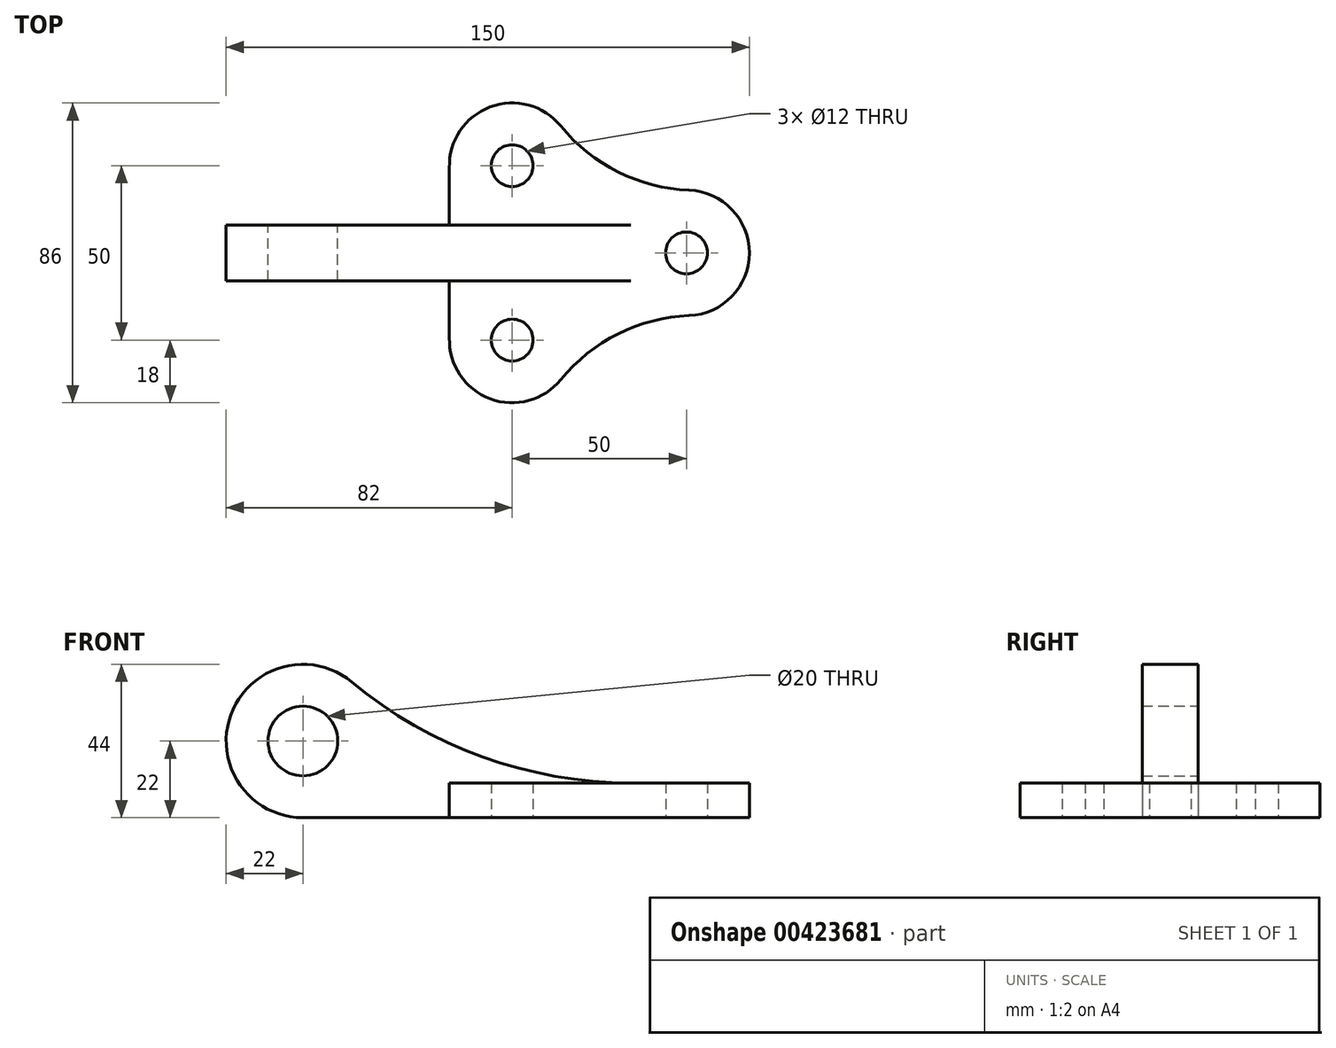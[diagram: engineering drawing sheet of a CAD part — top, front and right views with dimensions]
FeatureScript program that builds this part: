
annotation { "Feature Type Name" : "Feature", "Feature Type Description" : "" }
export const myFeature = defineFeature(function(context is Context, id is Id, definition is map)
    precondition{}
    {
        {
            var Q0;
            Q0=qCreatedBy(makeId("Top.planeOp"),FACE);
            var sketch = newSketch(context, id + "F0", { "sketchPlane" : qUnion([Q0])});
            skCircle(sketch, "E0", {"center": v(0, 0) * mm, "radius": 18 * mm});
            skCircle(sketch, "E1", {"center": v(-50, 25) * mm, "radius": 18 * mm});
            skCircle(sketch, "E2", {"center": v(-50, -25) * mm, "radius": 18 * mm});
            skLineSegment(sketch, "E3", {"start": v(-50, 25) * mm, "end": v(-50, -25) * mm});
            skLineSegment(sketch, "E4", {"start": v(0, 0) * mm, "end": v(-50, 0) * mm});
            skLineSegment(sketch, "E5", {"start": v(-68, 24.41) * mm, "end": v(-68, -25.59) * mm});
            skArc(sketch, "E6.MirrorCS", {"start": v(0.72, 17.99) * mm, "mid": v(-19.64, 23.22) * mm, "end": v(-36.04, 36.37) * mm});
            skCircle(sketch, "E7", {"center": v(-50, 25) * mm, "radius": 6 * mm});
            skCircle(sketch, "E8", {"center": v(-50, -25) * mm, "radius": 6 * mm});
            skCircle(sketch, "E9", {"center": v(0, 0) * mm, "radius": 6 * mm});
            skArc(sketch, "E10", {"start": v(0.72, -17.99) * mm, "mid": v(-19.64, -23.22) * mm, "end": v(-36.04, -36.37) * mm});
            skSolve(sketch);
        }
        {
            var Q0;
            Q0 = qSketchRegion(id + "F0", true);
            extrude(context, id + "F1", {"entities" : qUnion([Q0]), "depth" : 10 * mm});
        }
        {
            var Q0;
            Q0=qCreatedBy(makeId("Front.planeOp"),FACE);
            var sketch = newSketch(context, id + "F2", { "sketchPlane" : qUnion([Q0])});
            skCircle(sketch, "E11", {"center": v(-110, 22) * mm, "radius": 22 * mm});
            skLineSegment(sketch, "E12", {"start": v(0, 0) * mm, "end": v(-110.13, 0) * mm});
            skArc(sketch, "E13", {"start": v(-95.93, 38.91) * mm, "mid": v(-58.49, 17.45) * mm, "end": v(-15.98, 10) * mm});
            skPoint(sketch, "E14.orphan", {"position": v(0.72, 10) * mm});
            skLineSegment(sketch, "E15", {"start": v(-15.98, 10) * mm, "end": v(-15.98, 0) * mm});
            skPoint(sketch, "E16.0.end.orphan", {"position": v(-36.04, 10) * mm});
            skCircle(sketch, "E17", {"center": v(-110, 22) * mm, "radius": 10 * mm});
            skSolve(sketch);
        }
        {
            var Q0;
            Q0 = qSketchRegion(id + "F2", true);
            extrude(context, id + "F3", {"entities" : qUnion([Q0]), "operationType" : NewBodyOperationType.ADD, "endBound" : BoundingType.SYMMETRIC, "depth" : 16 * mm});
        }
    });
